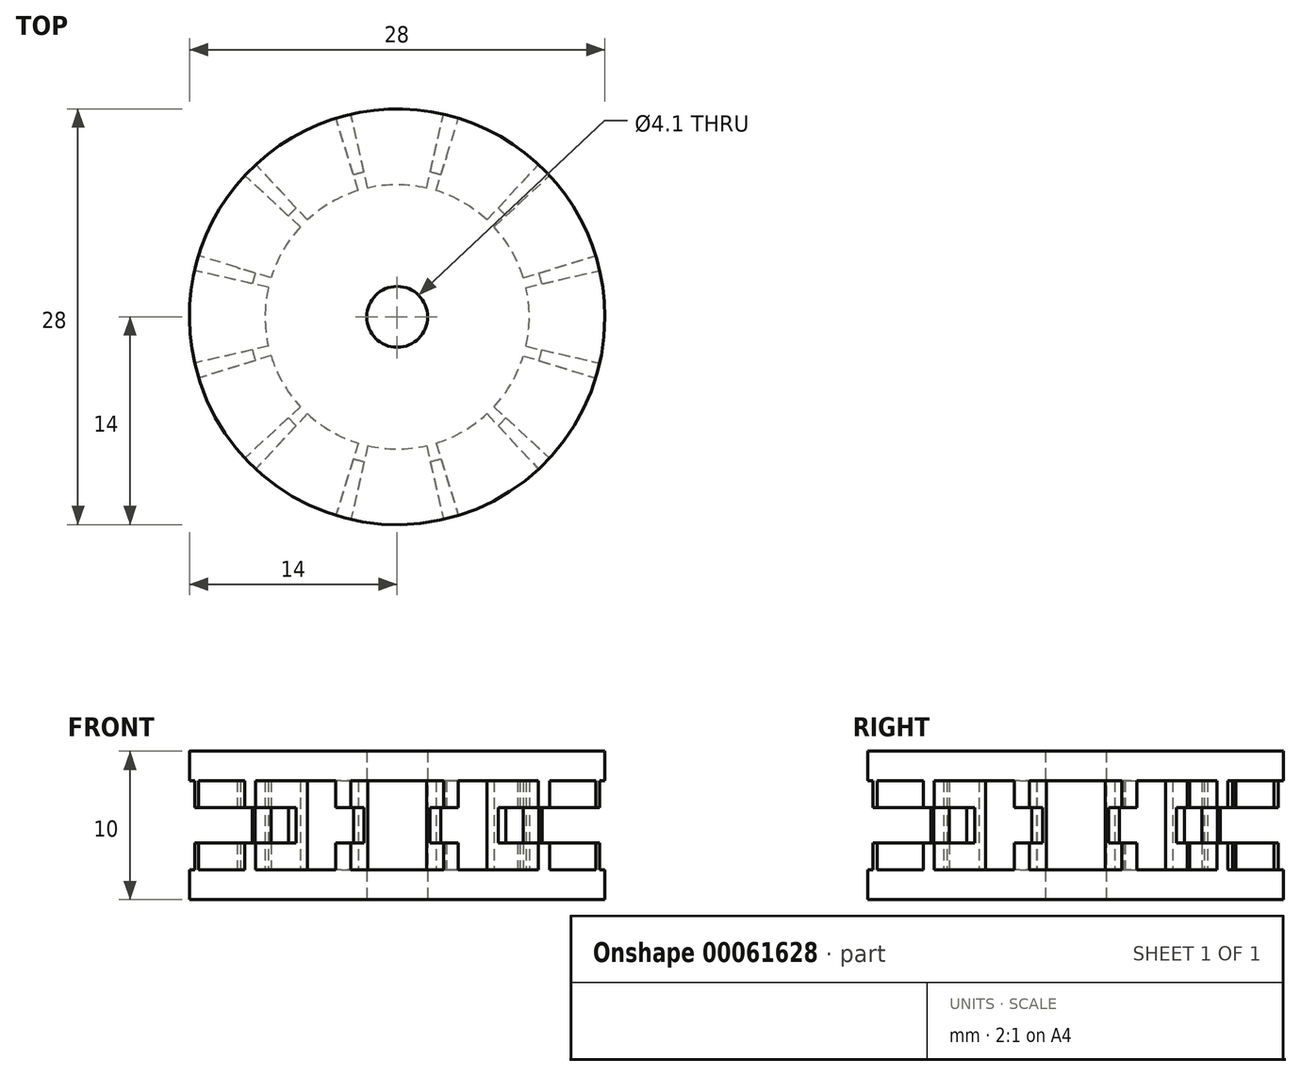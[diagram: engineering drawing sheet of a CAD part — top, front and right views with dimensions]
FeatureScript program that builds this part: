
annotation { "Feature Type Name" : "Feature", "Feature Type Description" : "" }
export const myFeature = defineFeature(function(context is Context, id is Id, definition is map)
    precondition{}
    {
        {
            var Q0;
            Q0=qCreatedBy(makeId("Top.planeOp"),FACE);
            var sketch = newSketch(context, id + "F0", { "sketchPlane" : qUnion([Q0])});
            skArc(sketch, "E0", {"start": v(-13.38, 4.13) * mm, "mid": v(-13.52, 3.63) * mm, "end": v(-13.65, 3.12) * mm});
            skArc(sketch, "E1.2.0", {"start": v(-10.94, 3.39) * mm, "mid": v(-10.75, 3.31) * mm, "end": v(-10.56, 3.26) * mm});
            skArc(sketch, "E1.10.0", {"start": v(8.4, 7.78) * mm, "mid": v(8.25, 7.65) * mm, "end": v(8.1, 7.51) * mm});
            skArc(sketch, "E1.11.0", {"start": v(3.39, 10.94) * mm, "mid": v(3.31, 10.75) * mm, "end": v(3.26, 10.56) * mm});
            skLineSegment(sketch, "E2", {"start": v(8.5, 2.62) * mm, "end": v(13.38, 4.12) * mm});
            skLineSegment(sketch, "E3", {"start": v(8.68, 1.98) * mm, "end": v(13.65, 3.11) * mm});
            skLineSegment(sketch, "E4.1.0", {"start": v(6.05, 6.52) * mm, "end": v(9.52, 10.26) * mm});
            skLineSegment(sketch, "E4.1.1", {"start": v(6.52, 6.05) * mm, "end": v(10.26, 9.52) * mm});
            skLineSegment(sketch, "E4.2.0", {"start": v(1.98, 8.68) * mm, "end": v(3.12, 13.65) * mm});
            skLineSegment(sketch, "E4.2.1", {"start": v(2.62, 8.5) * mm, "end": v(4.13, 13.38) * mm});
            skLineSegment(sketch, "E4.3.0", {"start": v(-2.62, 8.5) * mm, "end": v(-4.12, 13.38) * mm});
            skLineSegment(sketch, "E4.3.1", {"start": v(-1.98, 8.68) * mm, "end": v(-3.11, 13.65) * mm});
            skLineSegment(sketch, "E4.4.0", {"start": v(-6.52, 6.05) * mm, "end": v(-10.26, 9.52) * mm});
            skLineSegment(sketch, "E4.4.1", {"start": v(-6.05, 6.52) * mm, "end": v(-9.52, 10.26) * mm});
            skLineSegment(sketch, "E4.5.0", {"start": v(-8.68, 1.98) * mm, "end": v(-13.65, 3.12) * mm});
            skLineSegment(sketch, "E4.5.1", {"start": v(-8.5, 2.62) * mm, "end": v(-13.38, 4.13) * mm});
            skLineSegment(sketch, "E4.6.0", {"start": v(-8.5, -2.62) * mm, "end": v(-13.38, -4.12) * mm});
            skLineSegment(sketch, "E4.6.1", {"start": v(-8.68, -1.98) * mm, "end": v(-13.65, -3.11) * mm});
            skLineSegment(sketch, "E4.7.0", {"start": v(-6.05, -6.52) * mm, "end": v(-9.52, -10.26) * mm});
            skLineSegment(sketch, "E4.7.1", {"start": v(-6.52, -6.05) * mm, "end": v(-8.1, -7.51) * mm});
            skLineSegment(sketch, "E4.8.0", {"start": v(-1.98, -8.68) * mm, "end": v(-3.12, -13.65) * mm});
            skLineSegment(sketch, "E4.8.1", {"start": v(-2.62, -8.5) * mm, "end": v(-4.13, -13.38) * mm});
            skLineSegment(sketch, "E4.9.0", {"start": v(2.62, -8.5) * mm, "end": v(4.12, -13.38) * mm});
            skLineSegment(sketch, "E4.9.1", {"start": v(1.98, -8.68) * mm, "end": v(3.11, -13.65) * mm});
            skLineSegment(sketch, "E4.10.0", {"start": v(6.52, -6.05) * mm, "end": v(10.26, -9.52) * mm});
            skLineSegment(sketch, "E4.10.1", {"start": v(6.05, -6.52) * mm, "end": v(9.52, -10.26) * mm});
            skLineSegment(sketch, "E4.11.0", {"start": v(8.68, -1.98) * mm, "end": v(13.65, -3.12) * mm});
            skLineSegment(sketch, "E4.11.1", {"start": v(8.5, -2.62) * mm, "end": v(13.38, -4.13) * mm});
            skArc(sketch, "E5", {"start": v(6.52, -6.05) * mm, "mid": v(7.7, -4.45) * mm, "end": v(8.5, -2.62) * mm});
            skArc(sketch, "E6.trimOffspring", {"start": v(-10.88, 2.49) * mm, "mid": v(-11.02, 2.51) * mm, "end": v(-11.17, 2.53) * mm});
            skArc(sketch, "E7.trimOffspring", {"start": v(-13.65, -3.11) * mm, "mid": v(-13.52, -3.62) * mm, "end": v(-13.38, -4.12) * mm});
            skArc(sketch, "E8.trimOffspring", {"start": v(-10.26, -9.52) * mm, "mid": v(-9.9, -9.9) * mm, "end": v(-9.52, -10.26) * mm});
            skArc(sketch, "E9.trimOffspring", {"start": v(-3.11, 13.65) * mm, "mid": v(-3.62, 13.52) * mm, "end": v(-4.12, 13.38) * mm});
            skArc(sketch, "E10.trimOffspring", {"start": v(-9.52, 10.26) * mm, "mid": v(-9.9, 9.9) * mm, "end": v(-10.26, 9.52) * mm});
            skArc(sketch, "E11.trimOffspring", {"start": v(10.26, 9.52) * mm, "mid": v(9.9, 9.9) * mm, "end": v(9.52, 10.26) * mm});
            skArc(sketch, "E12.trimOffspring", {"start": v(10.67, 3.29) * mm, "mid": v(10.8, 3.33) * mm, "end": v(10.94, 3.39) * mm});
            skArc(sketch, "E13.trimOffspring", {"start": v(7.6, 8.18) * mm, "mid": v(7.69, 8.29) * mm, "end": v(7.78, 8.4) * mm});
            skArc(sketch, "E14.trimOffspring", {"start": v(-4.13, -13.38) * mm, "mid": v(-3.63, -13.52) * mm, "end": v(-3.12, -13.65) * mm});
            skArc(sketch, "E15.trimOffspring", {"start": v(3.11, -13.65) * mm, "mid": v(3.62, -13.52) * mm, "end": v(4.12, -13.38) * mm});
            skArc(sketch, "E16.trimOffspring", {"start": v(9.52, -10.26) * mm, "mid": v(9.9, -9.9) * mm, "end": v(10.26, -9.52) * mm});
            skArc(sketch, "E17.trimOffspring", {"start": v(13.38, -4.13) * mm, "mid": v(13.52, -3.63) * mm, "end": v(13.65, -3.12) * mm});
            skArc(sketch, "E18.trimOffspring", {"start": v(13.65, 3.11) * mm, "mid": v(13.52, 3.62) * mm, "end": v(13.38, 4.12) * mm});
            skLineSegment(sketch, "E19", {"start": v(4.13, 13.38) * mm, "end": v(3.12, 13.65) * mm});
            skArc(sketch, "E20.trimOffspring", {"start": v(-11.17, -2.53) * mm, "mid": v(-11.16, -2.54) * mm, "end": v(-11.16, -2.55) * mm});
            skArc(sketch, "E21.trimOffspring", {"start": v(-8.4, -7.77) * mm, "mid": v(-8.4, -7.78) * mm, "end": v(-8.39, -7.78) * mm});
            skArc(sketch, "E22.trimOffspring", {"start": v(-10.94, 3.39) * mm, "mid": v(-10.94, 3.38) * mm, "end": v(-10.94, 3.38) * mm});
            skArc(sketch, "E23.trimOffspring", {"start": v(8.4, 7.78) * mm, "mid": v(8.4, 7.78) * mm, "end": v(8.4, 7.79) * mm});
            skArc(sketch, "E24.trimOffspring", {"start": v(3.39, 10.94) * mm, "mid": v(3.38, 10.94) * mm, "end": v(3.38, 10.94) * mm});
            skArc(sketch, "E25.trimOffspring", {"start": v(10.94, 3.37) * mm, "mid": v(10.94, 3.38) * mm, "end": v(10.94, 3.39) * mm});
            skArc(sketch, "E26.trimOffspring", {"start": v(-10.94, -3.37) * mm, "mid": v(-10.94, -3.38) * mm, "end": v(-10.94, -3.39) * mm});
            skArc(sketch, "E27.trimOffspring", {"start": v(-11.16, 2.55) * mm, "mid": v(-11.16, 2.54) * mm, "end": v(-11.17, 2.53) * mm});
            skArc(sketch, "E28.trimOffspring", {"start": v(2.62, -8.5) * mm, "mid": v(4.45, -7.7) * mm, "end": v(6.05, -6.52) * mm});
            skArc(sketch, "E29.trimOffspring", {"start": v(-1.98, -8.68) * mm, "mid": v(0, -8.9) * mm, "end": v(1.98, -8.68) * mm});
            skArc(sketch, "E30.trimOffspring", {"start": v(-6.05, -6.52) * mm, "mid": v(-4.45, -7.7) * mm, "end": v(-2.62, -8.5) * mm});
            skArc(sketch, "E31.trimOffspring", {"start": v(-8.5, -2.62) * mm, "mid": v(-7.7, -4.45) * mm, "end": v(-6.52, -6.05) * mm});
            skArc(sketch, "E32.trimOffspring", {"start": v(-8.68, 1.98) * mm, "mid": v(-8.9, 0) * mm, "end": v(-8.68, -1.98) * mm});
            skArc(sketch, "E33.trimOffspring", {"start": v(-6.52, 6.05) * mm, "mid": v(-7.7, 4.45) * mm, "end": v(-8.5, 2.62) * mm});
            skArc(sketch, "E34.trimOffspring", {"start": v(-2.62, 8.5) * mm, "mid": v(-4.45, 7.7) * mm, "end": v(-6.05, 6.52) * mm});
            skArc(sketch, "E35.trimOffspring", {"start": v(1.98, 8.68) * mm, "mid": v(0, 8.9) * mm, "end": v(-1.98, 8.68) * mm});
            skArc(sketch, "E36.trimOffspring", {"start": v(6.05, 6.52) * mm, "mid": v(4.45, 7.7) * mm, "end": v(2.62, 8.5) * mm});
            skArc(sketch, "E37.trimOffspring", {"start": v(8.5, 2.62) * mm, "mid": v(7.7, 4.45) * mm, "end": v(6.52, 6.05) * mm});
            skArc(sketch, "E38.trimOffspring", {"start": v(8.68, -1.98) * mm, "mid": v(8.9, 0) * mm, "end": v(8.68, 1.98) * mm});
            skLineSegment(sketch, "E39.trimOffspring", {"start": v(-8.39, -7.78) * mm, "end": v(-10.26, -9.52) * mm});
            skLineSegment(sketch, "E40", {"start": v(-8.39, -7.78) * mm, "end": v(-8.1, -7.51) * mm});
            skSolve(sketch);
        }
        {
            var Q0;
            {var subQ15=sQuery(id+"F0.wireOp",EDGE,"E0");Q0=makeQuery(id+"F0.imprint","IMPRINT",FACE,{"disambiguationData":[TD([[makeQuery(id+"F0.imprint","IMPRINT",EDGE,{"derivedFrom":subQ15}),1.0]])]});}
            extrude(context, id + "F1", {"entities" : qUnion([Q0]), "depth" : 6 * mm});
        }
        {
            var Q0;
            Q0=makeQuery(id+"F1.opExtrude","SWEPT_FACE",FACE,{"disambiguationData":[OSD([sQuery(id+"F0.wireOp",EDGE,"E3")])]});
            var sketch = newSketch(context, id + "F2", { "sketchPlane" : qUnion([Q0])});
            skLineSegment(sketch, "E41.bottom", {"start": v(14, 4.2) * mm, "end": v(10, 4.2) * mm});
            skLineSegment(sketch, "E41.top", {"start": v(14, 1.8) * mm, "end": v(10, 1.8) * mm});
            skLineSegment(sketch, "E41.left", {"start": v(14, 4.2) * mm, "end": v(14, 1.8) * mm});
            skLineSegment(sketch, "E41.right", {"start": v(10, 4.2) * mm, "end": v(10, 1.8) * mm});
            skSolve(sketch);
        }
        {
            var Q0;
            Q0=qCreatedBy(makeId("Front.planeOp"),FACE);
            var sketch = newSketch(context, id + "F3", { "sketchPlane" : qUnion([Q0])});
            skLineSegment(sketch, "E42", {"start": v(0, 26.44) * mm, "end": v(0, -15.35) * mm});
            skSolve(sketch);
        }
        {
            var Q0;
            Q0 = qSketchRegion(id + "F2", true);
            var Q1;
            Q1=sQuery(id+"F3.wireOp",EDGE,"E42");
            revolve(context, id + "F4", {"operationType" : NewBodyOperationType.REMOVE, "entities" : qUnion([Q0]), "axis" : qUnion([Q1]), "revolveType" : RevolveType.FULL, "oppositeDirection" : true});
        }
        {
            var Q0;
            Q0=makeQuery(id+"F1.opExtrude","CAP_FACE",FACE,{"disambiguationData":[OSD([sQuery(id+"F0.wireOp",EDGE,"E0"),sQuery(id+"F0.wireOp",EDGE,"E1.2.0"),sQuery(id+"F0.wireOp",EDGE,"E1.10.0"),sQuery(id+"F0.wireOp",EDGE,"E1.11.0"),sQuery(id+"F0.wireOp",EDGE,"E2"),sQuery(id+"F0.wireOp",EDGE,"E3"),sQuery(id+"F0.wireOp",EDGE,"E4.1.0"),sQuery(id+"F0.wireOp",EDGE,"E4.1.1"),sQuery(id+"F0.wireOp",EDGE,"E4.2.0"),sQuery(id+"F0.wireOp",EDGE,"E4.2.1"),sQuery(id+"F0.wireOp",EDGE,"E4.3.0"),sQuery(id+"F0.wireOp",EDGE,"E4.3.1"),sQuery(id+"F0.wireOp",EDGE,"E4.4.0"),sQuery(id+"F0.wireOp",EDGE,"E4.4.1"),sQuery(id+"F0.wireOp",EDGE,"E4.5.0"),sQuery(id+"F0.wireOp",EDGE,"E4.5.1"),sQuery(id+"F0.wireOp",EDGE,"E4.6.0"),sQuery(id+"F0.wireOp",EDGE,"E4.6.1"),sQuery(id+"F0.wireOp",EDGE,"E4.7.0"),sQuery(id+"F0.wireOp",EDGE,"E4.7.1"),sQuery(id+"F0.wireOp",EDGE,"E4.8.0"),sQuery(id+"F0.wireOp",EDGE,"E4.8.1"),sQuery(id+"F0.wireOp",EDGE,"E4.9.0"),sQuery(id+"F0.wireOp",EDGE,"E4.9.1"),sQuery(id+"F0.wireOp",EDGE,"E4.10.0"),sQuery(id+"F0.wireOp",EDGE,"E4.10.1"),sQuery(id+"F0.wireOp",EDGE,"E4.11.0"),sQuery(id+"F0.wireOp",EDGE,"E4.11.1"),sQuery(id+"F0.wireOp",EDGE,"E5"),sQuery(id+"F0.wireOp",EDGE,"E7.trimOffspring"),sQuery(id+"F0.wireOp",EDGE,"E8.trimOffspring"),sQuery(id+"F0.wireOp",EDGE,"E9.trimOffspring"),sQuery(id+"F0.wireOp",EDGE,"E10.trimOffspring"),sQuery(id+"F0.wireOp",EDGE,"E11.trimOffspring"),sQuery(id+"F0.wireOp",EDGE,"E14.trimOffspring"),sQuery(id+"F0.wireOp",EDGE,"E15.trimOffspring"),sQuery(id+"F0.wireOp",EDGE,"E16.trimOffspring"),sQuery(id+"F0.wireOp",EDGE,"E17.trimOffspring"),sQuery(id+"F0.wireOp",EDGE,"E18.trimOffspring"),sQuery(id+"F0.wireOp",EDGE,"E19"),sQuery(id+"F0.wireOp",EDGE,"E28.trimOffspring"),sQuery(id+"F0.wireOp",EDGE,"E29.trimOffspring"),sQuery(id+"F0.wireOp",EDGE,"E30.trimOffspring"),sQuery(id+"F0.wireOp",EDGE,"E31.trimOffspring"),sQuery(id+"F0.wireOp",EDGE,"E32.trimOffspring"),sQuery(id+"F0.wireOp",EDGE,"E33.trimOffspring"),sQuery(id+"F0.wireOp",EDGE,"E34.trimOffspring"),sQuery(id+"F0.wireOp",EDGE,"E35.trimOffspring"),sQuery(id+"F0.wireOp",EDGE,"E36.trimOffspring"),sQuery(id+"F0.wireOp",EDGE,"E37.trimOffspring"),sQuery(id+"F0.wireOp",EDGE,"E38.trimOffspring"),sQuery(id+"F0.wireOp",EDGE,"E39.trimOffspring"),sQuery(id+"F0.wireOp",EDGE,"E40")])],"isStart":false});
            var sketch = newSketch(context, id + "F5", { "sketchPlane" : qUnion([Q0])});
            skCircle(sketch, "E43", {"center": v(0, 0) * mm, "radius": 14 * mm});
            skSolve(sketch);
        }
        {
            var Q0;
            Q0 = qSketchRegion(id + "F5", true);
            extrude(context, id + "F6", {"entities" : qUnion([Q0]), "operationType" : NewBodyOperationType.ADD, "depth" : 2 * mm});
        }
        {
            var Q0;
            Q0=makeQuery(id+"F1.opExtrude","CAP_FACE",FACE,{"disambiguationData":[OSD([sQuery(id+"F0.wireOp",EDGE,"E0"),sQuery(id+"F0.wireOp",EDGE,"E1.2.0"),sQuery(id+"F0.wireOp",EDGE,"E1.10.0"),sQuery(id+"F0.wireOp",EDGE,"E1.11.0"),sQuery(id+"F0.wireOp",EDGE,"E2"),sQuery(id+"F0.wireOp",EDGE,"E3"),sQuery(id+"F0.wireOp",EDGE,"E4.1.0"),sQuery(id+"F0.wireOp",EDGE,"E4.1.1"),sQuery(id+"F0.wireOp",EDGE,"E4.2.0"),sQuery(id+"F0.wireOp",EDGE,"E4.2.1"),sQuery(id+"F0.wireOp",EDGE,"E4.3.0"),sQuery(id+"F0.wireOp",EDGE,"E4.3.1"),sQuery(id+"F0.wireOp",EDGE,"E4.4.0"),sQuery(id+"F0.wireOp",EDGE,"E4.4.1"),sQuery(id+"F0.wireOp",EDGE,"E4.5.0"),sQuery(id+"F0.wireOp",EDGE,"E4.5.1"),sQuery(id+"F0.wireOp",EDGE,"E4.6.0"),sQuery(id+"F0.wireOp",EDGE,"E4.6.1"),sQuery(id+"F0.wireOp",EDGE,"E4.7.0"),sQuery(id+"F0.wireOp",EDGE,"E4.7.1"),sQuery(id+"F0.wireOp",EDGE,"E4.8.0"),sQuery(id+"F0.wireOp",EDGE,"E4.8.1"),sQuery(id+"F0.wireOp",EDGE,"E4.9.0"),sQuery(id+"F0.wireOp",EDGE,"E4.9.1"),sQuery(id+"F0.wireOp",EDGE,"E4.10.0"),sQuery(id+"F0.wireOp",EDGE,"E4.10.1"),sQuery(id+"F0.wireOp",EDGE,"E4.11.0"),sQuery(id+"F0.wireOp",EDGE,"E4.11.1"),sQuery(id+"F0.wireOp",EDGE,"E5"),sQuery(id+"F0.wireOp",EDGE,"E7.trimOffspring"),sQuery(id+"F0.wireOp",EDGE,"E8.trimOffspring"),sQuery(id+"F0.wireOp",EDGE,"E9.trimOffspring"),sQuery(id+"F0.wireOp",EDGE,"E10.trimOffspring"),sQuery(id+"F0.wireOp",EDGE,"E11.trimOffspring"),sQuery(id+"F0.wireOp",EDGE,"E14.trimOffspring"),sQuery(id+"F0.wireOp",EDGE,"E15.trimOffspring"),sQuery(id+"F0.wireOp",EDGE,"E16.trimOffspring"),sQuery(id+"F0.wireOp",EDGE,"E17.trimOffspring"),sQuery(id+"F0.wireOp",EDGE,"E18.trimOffspring"),sQuery(id+"F0.wireOp",EDGE,"E19"),sQuery(id+"F0.wireOp",EDGE,"E28.trimOffspring"),sQuery(id+"F0.wireOp",EDGE,"E29.trimOffspring"),sQuery(id+"F0.wireOp",EDGE,"E30.trimOffspring"),sQuery(id+"F0.wireOp",EDGE,"E31.trimOffspring"),sQuery(id+"F0.wireOp",EDGE,"E32.trimOffspring"),sQuery(id+"F0.wireOp",EDGE,"E33.trimOffspring"),sQuery(id+"F0.wireOp",EDGE,"E34.trimOffspring"),sQuery(id+"F0.wireOp",EDGE,"E35.trimOffspring"),sQuery(id+"F0.wireOp",EDGE,"E36.trimOffspring"),sQuery(id+"F0.wireOp",EDGE,"E37.trimOffspring"),sQuery(id+"F0.wireOp",EDGE,"E38.trimOffspring"),sQuery(id+"F0.wireOp",EDGE,"E39.trimOffspring"),sQuery(id+"F0.wireOp",EDGE,"E40")])],"isStart":true});
            var sketch = newSketch(context, id + "F7", { "sketchPlane" : qUnion([Q0])});
            skCircle(sketch, "E44", {"center": v(0, 0) * mm, "radius": 14 * mm});
            skSolve(sketch);
        }
        {
            var Q0;
            Q0 = qSketchRegion(id + "F7", true);
            extrude(context, id + "F8", {"entities" : qUnion([Q0]), "operationType" : NewBodyOperationType.ADD, "depth" : 2 * mm});
        }
        {
            var Q0;
            Q0=makeQuery(id+"F8.opExtrude","CAP_FACE",FACE,{"disambiguationData":[OSD([sQuery(id+"F7.wireOp",EDGE,"E44")])],"isStart":false});
            var sketch = newSketch(context, id + "F9", { "sketchPlane" : qUnion([Q0])});
            skCircle(sketch, "E45", {"center": v(0, 0) * mm, "radius": 2.05 * mm});
            skSolve(sketch);
        }
        {
            var Q0;
            Q0=makeQuery(id+"F9.imprint","IMPRINT",FACE,{"disambiguationData":[TD([[makeQuery(id+"F9.imprint","IMPRINT",EDGE,{"derivedFrom":sQuery(id+"F9.wireOp",EDGE,"E45")}),1.0]])]});
            extrude(context, id + "F10", {"entities" : qUnion([Q0]), "operationType" : NewBodyOperationType.REMOVE, "endBound" : BoundingType.THROUGH_ALL, "oppositeDirection" : true, "depth" : 25 * mm});
        }
    });
